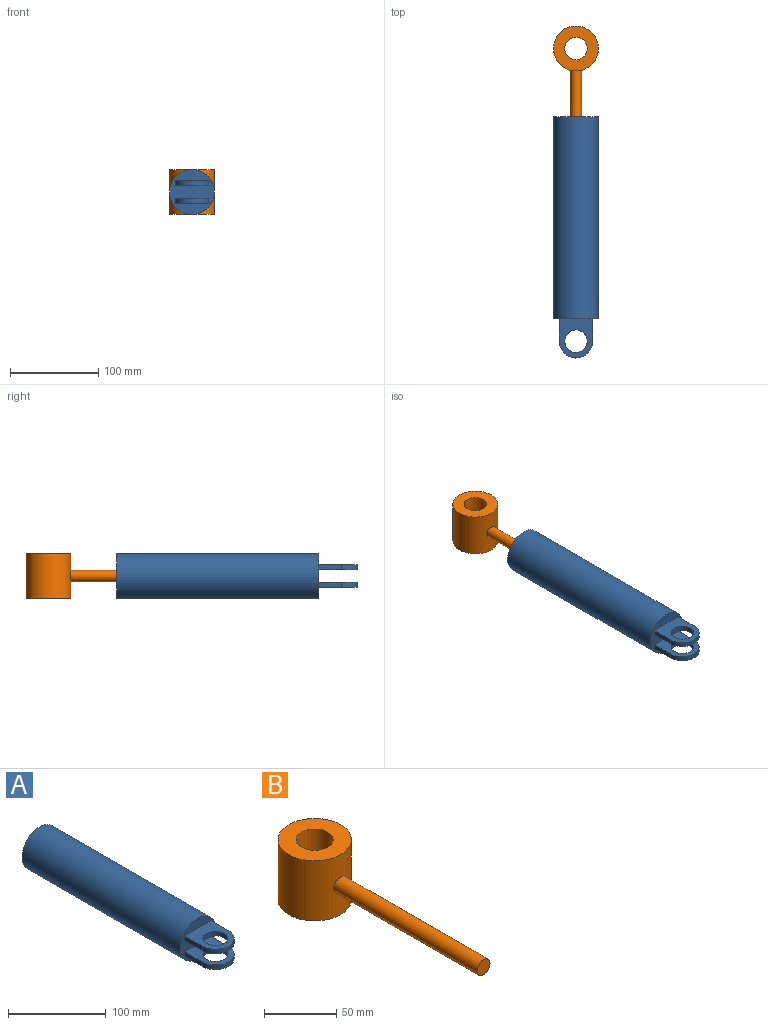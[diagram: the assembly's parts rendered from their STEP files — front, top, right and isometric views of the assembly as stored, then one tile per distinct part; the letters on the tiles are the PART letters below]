
ASSEMBLY  parts=2 mates=1
PART A: 17 faces, bbox 50.8x273.1x50.8 mm
  f0: plane 25.4x5.72mm, normal (1,0,0), area 145.2mm2, adj f7,f12,f13,f16
  f1: plane 25.4x5.72mm, normal (-1,0,0), area 145.2mm2, adj f3,f7,f14,f15
  f2: cylinder r=12.7mm len=25.4mm, axis (0,0,-1), area 456mm2, adj f14,f15
  f3: cylinder r=19.05mm len=38.1mm, axis (0,0,-1), area 342mm2, adj f1,f9,f14,f15
  f4: cylinder r=10.16mm len=76.2mm, axis (0,1,0), area 4864.4mm2, adj f6,f8
  f5: cylinder r=25.4mm len=228.6mm, axis (0,1,0), area 36482.9mm2, adj f6,f7
  f6: plane 50.8x50.8mm, normal (0,1,0), area 1702.5mm2, adj f4,f5
  f7: plane 50.8x50.8mm, normal (0,-1,0), area 1591.3mm2, adj f0,f1,f5,f9,f10,f13,f14,f15
  f8: plane 20.32x20.32mm, normal (0,1,0), area 324.3mm2, adj f4
  f9: plane 25.4x5.72mm, normal (1,0,0), area 145.2mm2, adj f3,f7,f14,f15
  f10: plane 25.4x5.72mm, normal (-1,0,0), area 145.2mm2, adj f7,f12,f13,f16
  f11: cylinder r=12.7mm len=25.4mm, axis (0,0,-1), area 456mm2, adj f13,f16
  f12: cylinder r=19.05mm len=38.1mm, axis (0,0,-1), area 342mm2, adj f0,f10,f13,f16
  f13: plane 44.45x38.1mm, normal (0,0,1), area 1031.1mm2, adj f0,f7,f10,f11,f12
  f14: plane 44.45x38.1mm, normal (0,0,-1), area 1031.1mm2, adj f1,f2,f3,f7,f9
  f15: plane 44.45x38.1mm, normal (0,0,1), area 1031.1mm2, adj f1,f2,f3,f7,f9
  f16: plane 44.45x38.1mm, normal (0,0,-1), area 1031.1mm2, adj f0,f7,f10,f11,f12
PART B: 6 faces, bbox 50.8x190.5x50.8 mm
  f0: cylinder r=6.35mm len=140.51mm, axis (0,1,0), area 5589.8mm2, adj f1,f2
  f1: plane 12.7x12.7mm, normal (0,-1,0), area 126.7mm2, adj f0
  f2: cylinder r=25.4mm len=50.8mm, axis (0,0,-1), area 7979.7mm2, adj f0,f4,f5
  f3: cylinder r=12.7mm len=50.8mm, axis (0,0,-1), area 4053.7mm2, adj f4,f5
  f4: plane 50.8x50.8mm, normal (0,0,1), area 1520.1mm2, adj f2,f3
  f5: plane 50.8x50.8mm, normal (0,0,-1), area 1520.1mm2, adj f2,f3
PLACE A at identity
PLACE B t=(0,-88.07,0)mm
MATE cylindrical B.f0 <-> A.f4  axis (0,1,0) through (0,-169.79,0)mm
